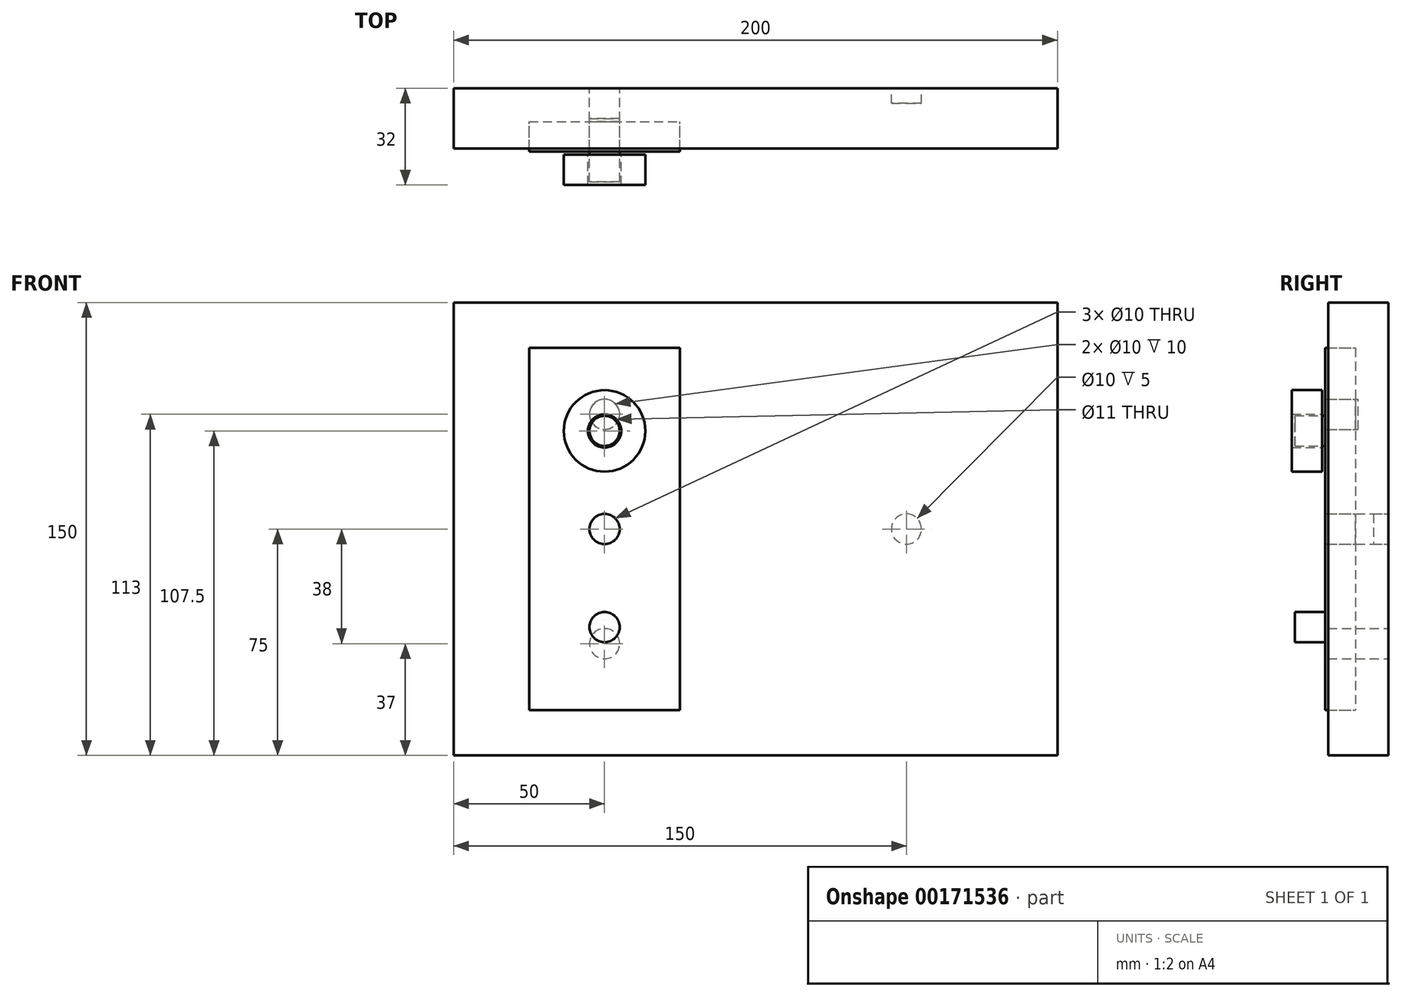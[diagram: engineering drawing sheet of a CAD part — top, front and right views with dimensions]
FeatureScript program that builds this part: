
annotation { "Feature Type Name" : "Feature", "Feature Type Description" : "" }
export const myFeature = defineFeature(function(context is Context, id is Id, definition is map)
    precondition{}
    {
        {
            var Q0;
            Q0=qCreatedBy(makeId("Front.planeOp"),FACE);
            var sketch = newSketch(context, id + "F0", { "sketchPlane" : qUnion([Q0])});
            skLineSegment(sketch, "E0.bottom", {"start": v(100, 75) * mm, "end": v(-100, 75) * mm});
            skLineSegment(sketch, "E0.top", {"start": v(100, -75) * mm, "end": v(-100, -75) * mm});
            skLineSegment(sketch, "E0.left", {"start": v(100, 75) * mm, "end": v(100, -75) * mm});
            skLineSegment(sketch, "E0.right", {"start": v(-100, 75) * mm, "end": v(-100, -75) * mm});
            skPoint(sketch, "E0.middle", {"position": v(0, 0) * mm});
            skLineSegment(sketch, "E1.bottom", {"start": v(100, 19) * mm, "end": v(-100, 19) * mm, "construction": true});
            skLineSegment(sketch, "E1.top", {"start": v(100, -19) * mm, "end": v(-100, -19) * mm, "construction": true});
            skLineSegment(sketch, "E1.left", {"start": v(100, 19) * mm, "end": v(100, -19) * mm, "construction": true});
            skLineSegment(sketch, "E1.right", {"start": v(-100, 14.84) * mm, "end": v(-100, -19) * mm, "construction": true});
            skPoint(sketch, "E2", {"position": v(50, 0) * mm});
            skCircle(sketch, "E3", {"center": v(50, 0) * mm, "radius": 19 * mm, "construction": true});
            skPoint(sketch, "E4", {"position": v(-50, 0) * mm});
            skCircle(sketch, "E5", {"center": v(-50, 38) * mm, "radius": 5 * mm});
            skCircle(sketch, "E6.MirrorC", {"center": v(-50, -38) * mm, "radius": 5 * mm});
            skCircle(sketch, "E7", {"center": v(50, 0) * mm, "radius": 5 * mm});
            skCircle(sketch, "E8.MirrorC", {"center": v(-50, 0) * mm, "radius": 5 * mm});
            skSolve(sketch);
        }
        {
            var Q0;
            Q0=makeQuery(id+"F0.imprint","IMPRINT",FACE,{"disambiguationData":[TD([[makeQuery(id+"F0.imprint","IMPRINT",EDGE,{"derivedFrom":sQuery(id+"F0.wireOp",EDGE,"E0.bottom")}),1.0]])]});
            var Q1;
            Q1=makeQuery(id+"F0.imprint","IMPRINT",FACE,{"disambiguationData":[TD([[makeQuery(id+"F0.imprint","IMPRINT",EDGE,{"derivedFrom":sQuery(id+"F0.wireOp",EDGE,"E5")}),1.0]])]});
            var Q2;
            Q2=makeQuery(id+"F0.imprint","IMPRINT",FACE,{"disambiguationData":[TD([[makeQuery(id+"F0.imprint","IMPRINT",EDGE,{"derivedFrom":sQuery(id+"F0.wireOp",EDGE,"E6.MirrorC")}),-1.0]])]});
            extrude(context, id + "F1", {"entities" : qUnion([Q0, Q1, Q2]), "depth" : 10 * mm});
        }
        {
            var Q0;
            Q0=makeQuery(id+"F0.imprint","IMPRINT",FACE,{"disambiguationData":[TD([[makeQuery(id+"F0.imprint","IMPRINT",EDGE,{"derivedFrom":sQuery(id+"F0.wireOp",EDGE,"E8.MirrorC")}),-1.0]])]});
            var Q1;
            Q1=makeQuery(id+"F0.imprint","IMPRINT",FACE,{"disambiguationData":[TD([[makeQuery(id+"F0.imprint","IMPRINT",EDGE,{"derivedFrom":sQuery(id+"F0.wireOp",EDGE,"E7")}),1.0]])]});
            extrude(context, id + "F2", {"entities" : qUnion([Q0, Q1]), "operationType" : NewBodyOperationType.ADD, "depth" : 20 * mm});
        }
        {
            var Q0;
            {var subQ0=sQuery(id+"F0.wireOp",EDGE,"E8.MirrorC");Q0=makeQuery(id+"FzNsiysy4ztsOz8_2.boolean.opBoolean","MERGE",FACE,{"derivedFrom":[makeQuery(id+"F2.opExtrude","CAP_FACE",FACE,{"disambiguationData":[OSD([subQ0])],"isStart":false}),makeQuery(id+"FzNsiysy4ztsOz8_2.opExtrude","CAP_FACE",FACE,{"disambiguationData":[OSD([subQ0,sQuery(id+"FyUuvjiDZBKfdtO_2.wireOp",EDGE,"aoUqkZuc-UMUI-3g7E-gpQo-OfSRTUkAMcKX.bottom"),sQuery(id+"FyUuvjiDZBKfdtO_2.wireOp",EDGE,"aoUqkZuc-UMUI-3g7E-gpQo-OfSRTUkAMcKX.top"),sQuery(id+"FyUuvjiDZBKfdtO_2.wireOp",EDGE,"aoUqkZuc-UMUI-3g7E-gpQo-OfSRTUkAMcKX.left"),sQuery(id+"FyUuvjiDZBKfdtO_2.wireOp",EDGE,"aoUqkZuc-UMUI-3g7E-gpQo-OfSRTUkAMcKX.right")])],"isStart":false})]});}
            var sketch = newSketch(context, id + "F3", { "sketchPlane" : qUnion([Q0])});
            skPoint(sketch, "E9", {"position": v(-50, 0) * mm});
            skCircle(sketch, "E10", {"center": v(-50, 38) * mm, "radius": 5 * mm});
            skCircle(sketch, "E11.MirrorC", {"center": v(-50, -38) * mm, "radius": 5 * mm});
            skSolve(sketch);
        }
        {
            var Q0;
            Q0=makeQuery(id+"F1.opExtrude","CAP_FACE",FACE,{"disambiguationData":[OSD([sQuery(id+"F0.wireOp",EDGE,"E0.bottom"),sQuery(id+"F0.wireOp",EDGE,"E0.top"),sQuery(id+"F0.wireOp",EDGE,"E0.left"),sQuery(id+"F0.wireOp",EDGE,"E0.right"),sQuery(id+"F0.wireOp",EDGE,"E7"),sQuery(id+"F0.wireOp",EDGE,"E8.MirrorC")])],"isStart":false});
            cPlane(context, id + "F4", {"entities" : qUnion([Q0]), "cplaneType" : CPlaneType.OFFSET, "offset" : 1 * mm, "width" : 150 * mm, "height" : 150 * mm});
        }
        {
            var Q0;
            Q0=qCreatedBy(id+"F4.planeOp",FACE);
            var sketch = newSketch(context, id + "F5", { "sketchPlane" : qUnion([Q0])});
            skLineSegment(sketch, "E12.bottom", {"start": v(-75, 60) * mm, "end": v(-25, 60) * mm});
            skLineSegment(sketch, "E12.top", {"start": v(-75, -60) * mm, "end": v(-25, -60) * mm});
            skLineSegment(sketch, "E12.left", {"start": v(-75, 60) * mm, "end": v(-75, -60) * mm});
            skLineSegment(sketch, "E12.right", {"start": v(-25, 60) * mm, "end": v(-25, -60) * mm});
            skPoint(sketch, "E12.middle", {"position": v(-50, 0) * mm});
            skCircle(sketch, "E13", {"center": v(-50, 0) * mm, "radius": 5 * mm});
            skCircle(sketch, "E14", {"center": v(-50, -38) * mm, "radius": 5 * mm});
            skCircle(sketch, "E15.MirrorC", {"center": v(-50, 38) * mm, "radius": 5 * mm});
            skSolve(sketch);
        }
        {
            var Q0;
            Q0=makeQuery(id+"F5.imprint","IMPRINT",FACE,{"disambiguationData":[TD([[makeQuery(id+"F5.imprint","IMPRINT",EDGE,{"derivedFrom":sQuery(id+"F5.wireOp",EDGE,"E15.MirrorC")}),-1.0]])]});
            var Q1;
            Q1=makeQuery(id+"F5.imprint","IMPRINT",FACE,{"disambiguationData":[TD([[makeQuery(id+"F5.imprint","IMPRINT",EDGE,{"derivedFrom":sQuery(id+"F5.wireOp",EDGE,"E14")}),1.0]])]});
            var Q2;
            Q2=makeQuery(id+"F5.imprint","IMPRINT",FACE,{"disambiguationData":[TD([[makeQuery(id+"F5.imprint","IMPRINT",EDGE,{"derivedFrom":sQuery(id+"F5.wireOp",EDGE,"E12.bottom")}),-1.0]])]});
            extrude(context, id + "F6", {"entities" : qUnion([Q0, Q1, Q2]), "depth" : 10 * mm});
        }
        {
            var Q0;
            Q0=makeQuery(id+"F6.opExtrude","CAP_FACE",FACE,{"disambiguationData":[OSD([sQuery(id+"F5.wireOp",EDGE,"E12.bottom"),sQuery(id+"F5.wireOp",EDGE,"E12.top"),sQuery(id+"F5.wireOp",EDGE,"E12.left"),sQuery(id+"F5.wireOp",EDGE,"E12.right"),sQuery(id+"F5.wireOp",EDGE,"E13"),sQuery(id+"F5.wireOp",EDGE,"E14"),sQuery(id+"F5.wireOp",EDGE,"E15.MirrorC")])],"isStart":false});
            cPlane(context, id + "F7", {"entities" : qUnion([Q0]), "cplaneType" : CPlaneType.OFFSET, "offset" : 1 * mm, "width" : 150 * mm, "height" : 150 * mm});
        }
        {
            var Q0;
            Q0=qCreatedBy(id+"F7.planeOp",FACE);
            var sketch = newSketch(context, id + "F8", { "sketchPlane" : qUnion([Q0])});
            skCircle(sketch, "E16", {"center": v(-50, 32.5) * mm, "radius": 5.5 * mm});
            skCircle(sketch, "E17.0", {"center": v(-50, 32.5) * mm, "radius": 13.5 * mm});
            skSolve(sketch);
        }
        {
            var Q0;
            {var subQ0=sQuery(id+"F0.wireOp",EDGE,"E8.MirrorC");var subQ1=sQuery(id+"F0.wireOp",EDGE,"E7");Q0=makeQuery(id+"F2.boolean.opBoolean","MERGE",FACE,{"derivedFrom":[makeQuery(id+"F1.opExtrude","CAP_FACE",FACE,{"disambiguationData":[OSD([sQuery(id+"F0.wireOp",EDGE,"E0.bottom"),sQuery(id+"F0.wireOp",EDGE,"E0.top"),sQuery(id+"F0.wireOp",EDGE,"E0.left"),sQuery(id+"F0.wireOp",EDGE,"E0.right"),subQ1,subQ0])],"isStart":true}),makeQuery(id+"F2.opExtrude","CAP_FACE",FACE,{"disambiguationData":[OSD([subQ1])],"isStart":true}),makeQuery(id+"F2.opExtrude","CAP_FACE",FACE,{"disambiguationData":[OSD([subQ0])],"isStart":true})]});}
            var sketch = newSketch(context, id + "F9", { "sketchPlane" : qUnion([Q0])});
            skCircle(sketch, "E18", {"center": v(-50, 0) * mm, "radius": 5 * mm});
            skPoint(sketch, "E18.centerSnap0", {"position": v(-100, 0) * mm});
            skSolve(sketch);
        }
        {
            var Q0;
            Q0 = qSketchRegion(id + "F9", true);
            extrude(context, id + "F10", {"entities" : qUnion([Q0]), "operationType" : NewBodyOperationType.REMOVE, "oppositeDirection" : true, "depth" : 5 * mm});
        }
        {
            var Q0;
            Q0 = qSketchRegion(id + "F8", true);
            extrude(context, id + "F11", {"entities" : qUnion([Q0]), "depth" : 10 * mm});
        }
        {
            var Q0;
            Q0=makeQuery(id+"F6.opExtrude","CAP_FACE",FACE,{"disambiguationData":[OSD([sQuery(id+"F5.wireOp",EDGE,"E12.bottom"),sQuery(id+"F5.wireOp",EDGE,"E12.top"),sQuery(id+"F5.wireOp",EDGE,"E12.left"),sQuery(id+"F5.wireOp",EDGE,"E12.right"),sQuery(id+"F5.wireOp",EDGE,"E13")])],"isStart":false});
            var sketch = newSketch(context, id + "F12", { "sketchPlane" : qUnion([Q0])});
            skCircle(sketch, "E19", {"center": v(-50, 32.5) * mm, "radius": 5 * mm});
            skCircle(sketch, "E20.MirrorC", {"center": v(-50, -32.5) * mm, "radius": 5 * mm});
            skSolve(sketch);
        }
        {
            var Q0;
            Q0 = qSketchRegion(id + "F12", true);
            extrude(context, id + "F13", {"entities" : qUnion([Q0]), "operationType" : NewBodyOperationType.ADD, "depth" : 10 * mm});
        }
    });
